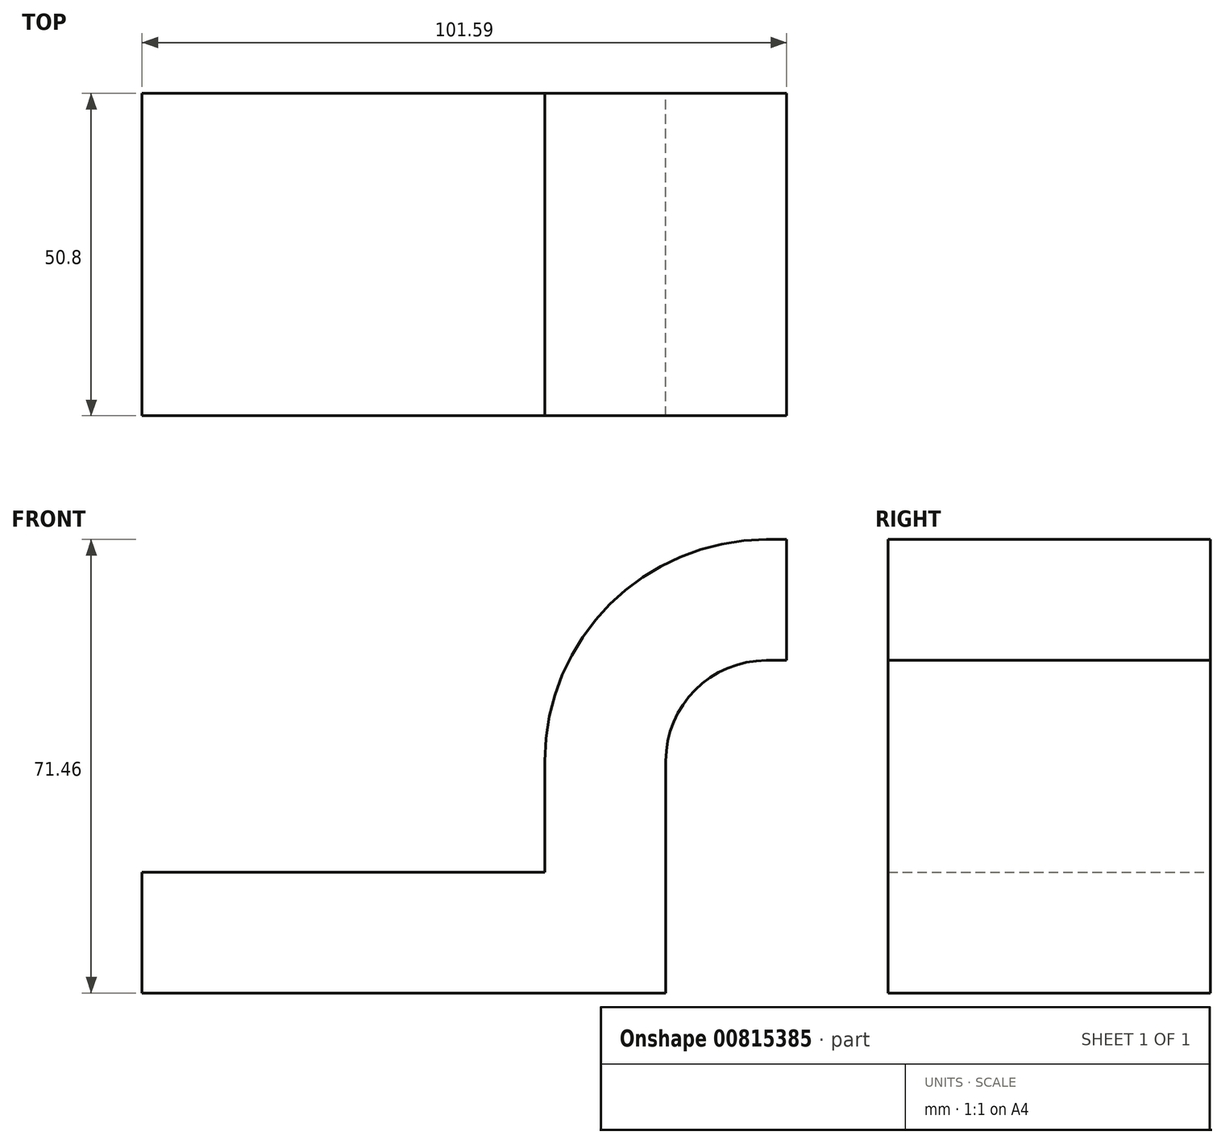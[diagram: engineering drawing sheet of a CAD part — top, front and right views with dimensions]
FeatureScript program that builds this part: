
annotation { "Feature Type Name" : "Feature", "Feature Type Description" : "" }
export const myFeature = defineFeature(function(context is Context, id is Id, definition is map)
    precondition{}
    {
        {
            var Q0;
            Q0=qCreatedBy(makeId("Front.planeOp"),FACE);
            var sketch = newSketch(context, id + "F0", { "sketchPlane" : qUnion([Q0])});
            skLineSegment(sketch, "E0.bottom", {"start": v(41.28, -9.52) * mm, "end": v(-41.28, -9.53) * mm});
            skLineSegment(sketch, "E0.top", {"start": v(41.28, 9.53) * mm, "end": v(-41.28, 9.53) * mm});
            skLineSegment(sketch, "E0.left", {"start": v(41.28, -9.52) * mm, "end": v(41.28, 9.53) * mm});
            skLineSegment(sketch, "E0.right", {"start": v(-41.28, -9.53) * mm, "end": v(-41.28, 9.53) * mm});
            skPoint(sketch, "E0.middle", {"position": v(0, 0) * mm});
            skLineSegment(sketch, "E1.bottom", {"start": v(111.13, 38.1) * mm, "end": v(60.33, 38.1) * mm});
            skLineSegment(sketch, "E1.top", {"start": v(111.13, 66.68) * mm, "end": v(60.33, 66.68) * mm});
            skLineSegment(sketch, "E1.left", {"start": v(111.13, 38.1) * mm, "end": v(111.13, 66.68) * mm});
            skLineSegment(sketch, "E1.right", {"start": v(60.33, 38.1) * mm, "end": v(60.33, 66.68) * mm});
            skPoint(sketch, "E1.middle", {"position": v(85.73, 52.39) * mm});
            skLineSegment(sketch, "E2", {"start": v(41.28, 9.53) * mm, "end": v(41.28, 27) * mm});
            skArc(sketch, "E3", {"start": v(41.27, 27) * mm, "mid": v(45.92, 38.23) * mm, "end": v(57.15, 42.88) * mm});
            skLineSegment(sketch, "E4", {"start": v(57.15, 42.88) * mm, "end": v(97.6, 42.88) * mm});
            skLineSegment(sketch, "E5.0", {"start": v(57.15, 61.93) * mm, "end": v(97.6, 61.93) * mm});
            skArc(sketch, "E5.1", {"start": v(22.23, 27) * mm, "mid": v(32.45, 51.7) * mm, "end": v(57.15, 61.93) * mm});
            skLineSegment(sketch, "E5.2", {"start": v(22.22, 9.53) * mm, "end": v(22.22, 27) * mm});
            skLineSegment(sketch, "E6", {"start": v(85.73, 38.1) * mm, "end": v(85.73, 66.68) * mm});
            skFitSpline(sketch, "E7", {"points": [v(57.15, 61.93) * mm, v(-41.28, 9.52) * mm], "startDerivative": vector(-158.1, 1.19) * mm, "endDerivative": vector(0.58, -106.38) * mm});
            skSolve(sketch);
        }
        {
            var Q0;
            Q0=makeQuery(id+"F0.imprint","IMPRINT",FACE,{"disambiguationData":[TD([[makeQuery(id+"F0.imprint","IMPRINT",EDGE,{"derivedFrom":sQuery(id+"F0.wireOp",EDGE,"E0.bottom")}),-1.0]])]});
            var Q1;
            {var subQ1=sQuery(id+"F0.wireOp",EDGE,"E2");Q1=makeQuery(id+"F0.imprint","IMPRINT",FACE,{"disambiguationData":[TD([[makeQuery(id+"F0.imprint","IMPRINT",EDGE,{"derivedFrom":subQ1}),1.0]])]});}
            extrude(context, id + "F1", {"entities" : qUnion([Q0, Q1]), "endBound" : BoundingType.SYMMETRIC, "depth" : 50.8 * mm, "offsetDistance" : 25.4 * mm});
        }
    });
